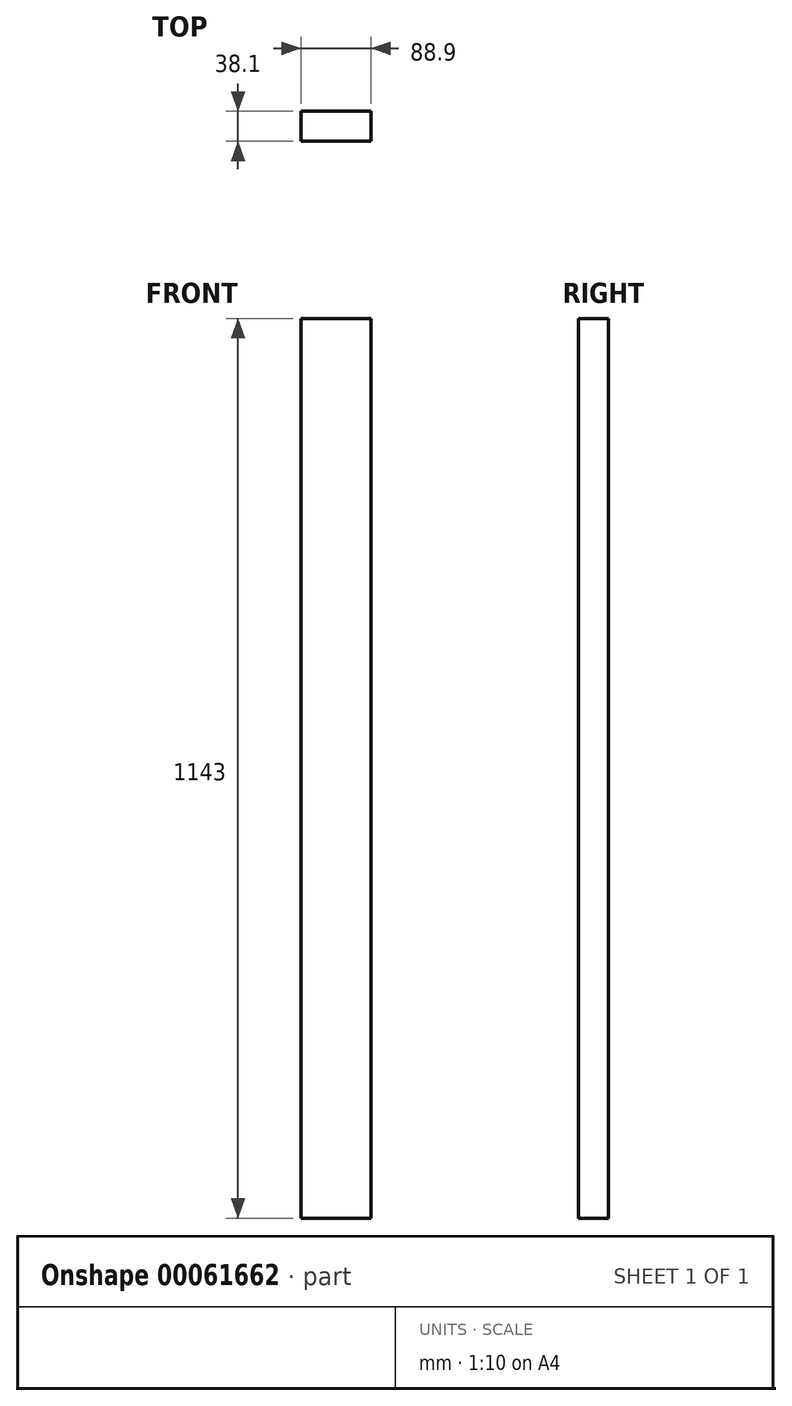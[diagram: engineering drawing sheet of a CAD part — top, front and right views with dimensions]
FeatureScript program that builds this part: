
annotation { "Feature Type Name" : "Feature", "Feature Type Description" : "" }
export const myFeature = defineFeature(function(context is Context, id is Id, definition is map)
    precondition{}
    {
        {
            var Q0;
            Q0=qCreatedBy(makeId("Top.planeOp"),FACE);
            var sketch = newSketch(context, id + "F0", { "sketchPlane" : qUnion([Q0])});
            skLineSegment(sketch, "E0.bottom", {"start": v(0, 0) * mm, "end": v(88.9, 0) * mm});
            skLineSegment(sketch, "E0.top", {"start": v(0, 38.1) * mm, "end": v(88.9, 38.1) * mm});
            skLineSegment(sketch, "E0.left", {"start": v(0, 0) * mm, "end": v(0, 38.1) * mm});
            skLineSegment(sketch, "E0.right", {"start": v(88.9, 0) * mm, "end": v(88.9, 38.1) * mm});
            skSolve(sketch);
        }
        {
            var Q0;
            Q0=qSketchRegion(id+"F0",true);
            extrude(context, id + "F1", {"entities" : qUnion([Q0]), "depth" : 1143 * mm});
        }
    });
